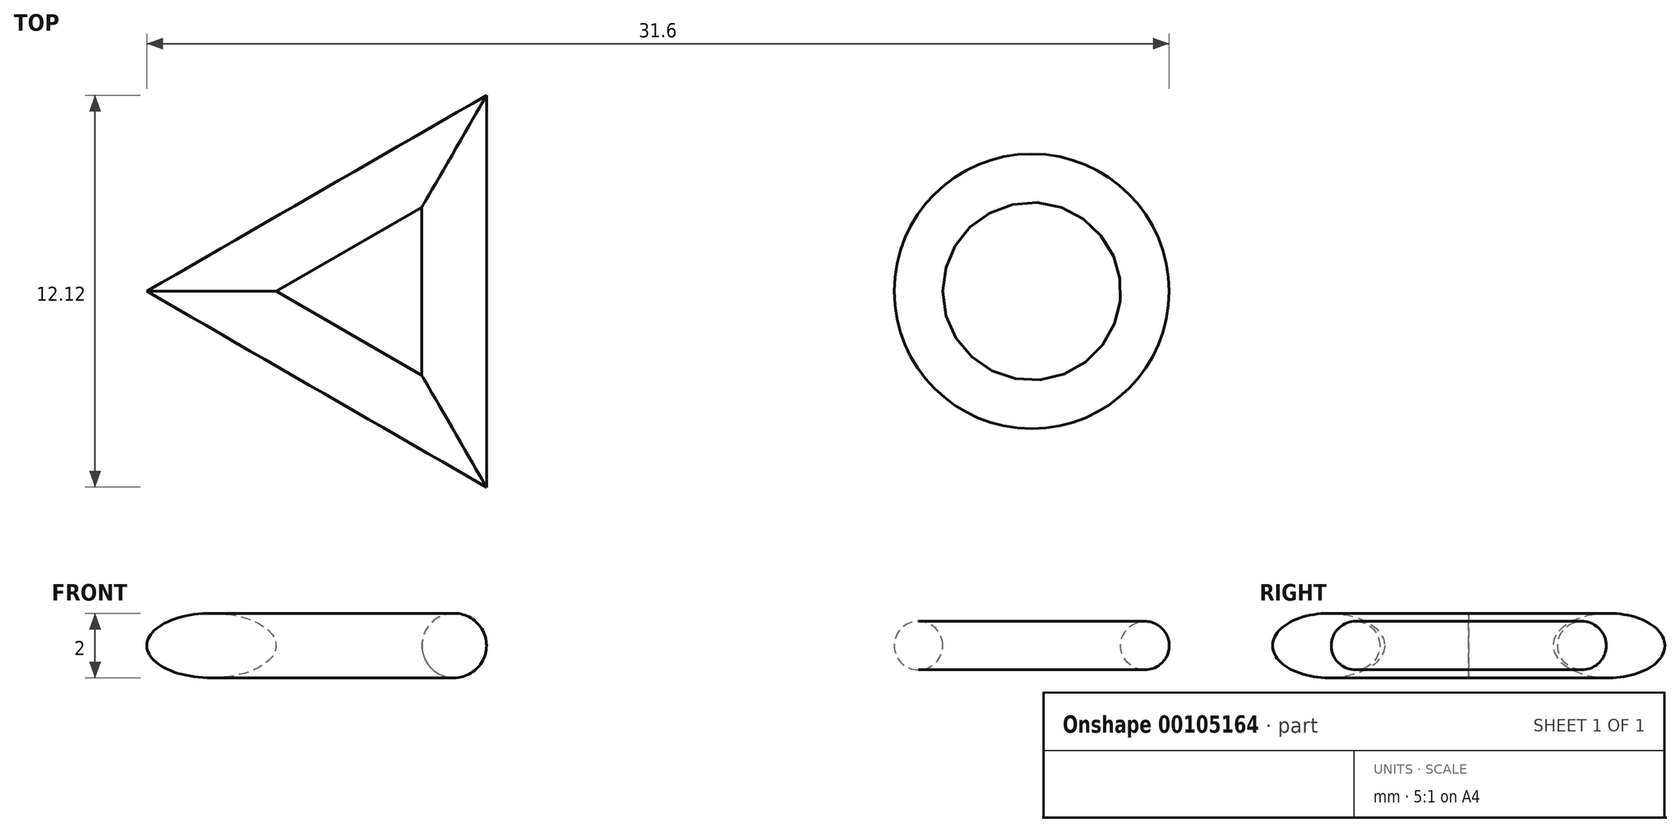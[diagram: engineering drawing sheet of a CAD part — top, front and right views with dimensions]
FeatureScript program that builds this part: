
annotation { "Feature Type Name" : "Feature", "Feature Type Description" : "" }
export const myFeature = defineFeature(function(context is Context, id is Id, definition is map)
    precondition{}
    {
        {
            var Q0;
            Q0=qCreatedBy(makeId("Front.planeOp"),FACE);
            var sketch = newSketch(context, id + "F0", { "sketchPlane" : qUnion([Q0])});
            skLineSegment(sketch, "E0", {"start": v(0, -3.98) * mm, "end": v(0, 4.87) * mm});
            skLineSegment(sketch, "E1", {"start": v(0, 0) * mm, "end": v(-3.5, 0) * mm});
            skCircle(sketch, "E2", {"center": v(-3.5, 0) * mm, "radius": 0.75 * mm});
            skSolve(sketch);
        }
        {
            var Q0;
            Q0=makeQuery(id+"F0.imprint","IMPRINT",FACE,{"disambiguationData":[TD([[makeQuery(id+"F0.imprint","IMPRINT",EDGE,{"derivedFrom":sQuery(id+"F0.wireOp",EDGE,"E2")}),1.0]])]});
            var Q1;
            Q1=sQuery(id+"F0.wireOp",EDGE,"E0");
            revolve(context, id + "F1", {"entities" : qUnion([Q0]), "axis" : qUnion([Q1]), "revolveType" : RevolveType.FULL});
        }
        {
            var Q0;
            Q0=qCreatedBy(makeId("Top.planeOp"),FACE);
            var sketch = newSketch(context, id + "F2", { "sketchPlane" : qUnion([Q0])});
            skCircle(sketch, "E3.cCircle", {"center": v(-20.35, 0) * mm, "radius": 5 * mm, "construction": true});
            skLineSegment(sketch, "E3.0", {"start": v(-25.35, 0) * mm, "end": v(-17.85, 4.33) * mm});
            skLineSegment(sketch, "E3.1", {"start": v(-17.85, 4.33) * mm, "end": v(-17.85, -4.33) * mm});
            skLineSegment(sketch, "E3.2", {"start": v(-17.85, -4.33) * mm, "end": v(-25.35, 0) * mm});
            skPoint(sketch, "E4.visualSharp", {"position": v(-17.85, 4.33) * mm});
            skLineSegment(sketch, "E4.filletArc", {"start": v(-17.85, 4.33) * mm, "end": v(-17.85, 4.33) * mm});
            skPoint(sketch, "E5.visualSharp", {"position": v(-17.85, -4.33) * mm});
            skLineSegment(sketch, "E5.filletArc", {"start": v(-17.85, -4.33) * mm, "end": v(-17.85, -4.33) * mm});
            skPoint(sketch, "E6.visualSharp", {"position": v(-25.35, 0) * mm});
            skLineSegment(sketch, "E6.filletArc", {"start": v(-25.35, 0) * mm, "end": v(-25.35, 0) * mm});
            skSolve(sketch);
        }
        {
            var Q0;
            Q0=qCreatedBy(makeId("Front.planeOp"),FACE);
            var sketch = newSketch(context, id + "F3", { "sketchPlane" : qUnion([Q0])});
            skCircle(sketch, "E7", {"center": v(-17.85, 0) * mm, "radius": 1 * mm});
            skSolve(sketch);
        }
        {
            var Q0;
            Q0 = qSketchRegion(id + "F3", true);
            var Q1;
            Q1 = qConstructionFilter(qBodyType(qCreatedBy(id + "F2" ,EDGE), BodyType.WIRE), ConstructionObject.NO);
            sweep(context, id + "F4", {"profiles" : qUnion([Q0]), "path" : qUnion([Q1])});
        }
    });
